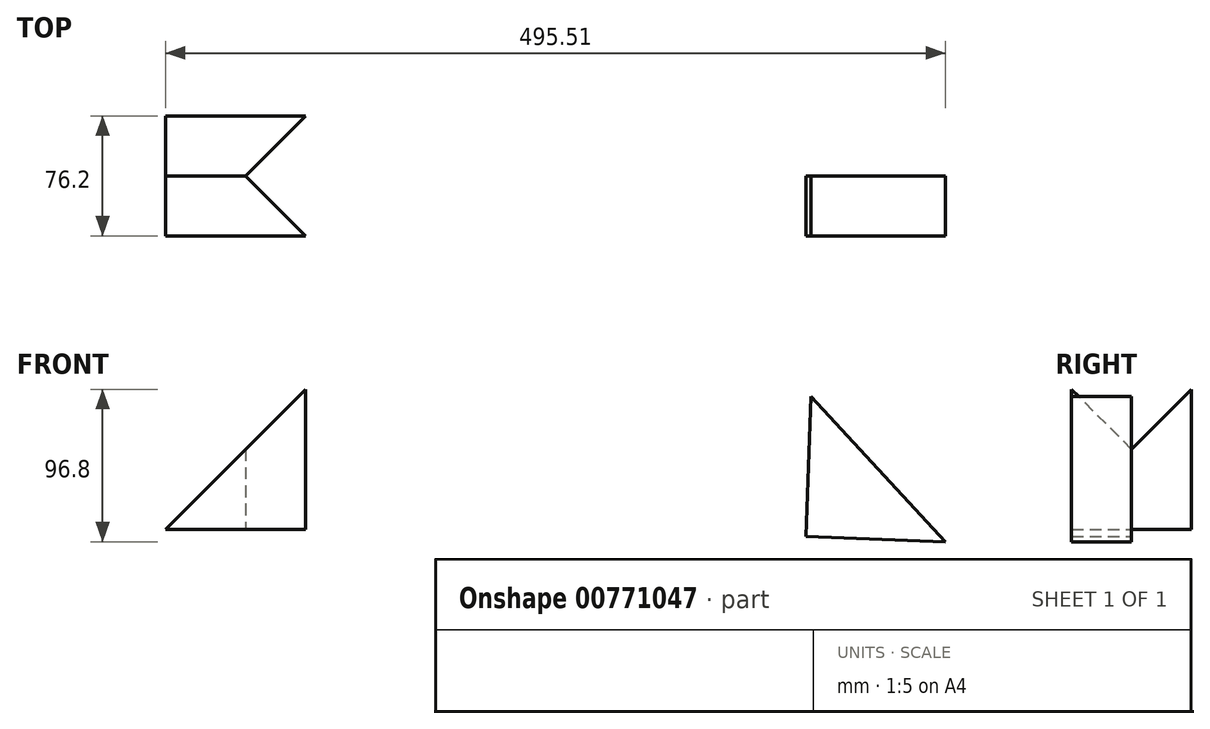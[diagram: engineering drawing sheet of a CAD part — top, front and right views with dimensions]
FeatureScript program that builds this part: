
annotation { "Feature Type Name" : "Feature", "Feature Type Description" : "" }
export const myFeature = defineFeature(function(context is Context, id is Id, definition is map)
    precondition{}
    {
        {
            var Q0;
            Q0=qCreatedBy(makeId("Front.planeOp"),FACE);
            var sketch = newSketch(context, id + "F0", { "sketchPlane" : qUnion([Q0])});
            skLineSegment(sketch, "E0", {"start": v(66.82, 257.53) * mm, "end": v(155.72, 257.53) * mm});
            skLineSegment(sketch, "E1", {"start": v(155.72, 257.53) * mm, "end": v(155.72, 346.43) * mm});
            skLineSegment(sketch, "E2", {"start": v(155.72, 346.43) * mm, "end": v(66.82, 257.53) * mm});
            skSolve(sketch);
        }
        {
            var Q0;
            Q0=makeQuery(id+"F0.imprint","IMPRINT",FACE,{"disambiguationData":[TD([[makeQuery(id+"F0.imprint","IMPRINT",EDGE,{"derivedFrom":sQuery(id+"F0.wireOp",EDGE,"E0")}),1.0]])]});
            extrude(context, id + "F1", {"entities" : qUnion([Q0]), "depth" : 38.1 * mm, "offsetDistance" : 25.4 * mm});
        }
        {
            var Q0;
            Q0=qCreatedBy(makeId("Front.planeOp"),FACE);
            var sketch = newSketch(context, id + "F2", { "sketchPlane" : qUnion([Q0])});
            skLineSegment(sketch, "E3", {"start": v(219.24, 257.56) * mm, "end": v(205.65, 358.25) * mm});
            skLineSegment(sketch, "E4", {"start": v(205.65, 358.25) * mm, "end": v(319.93, 271.16) * mm});
            skLineSegment(sketch, "E5", {"start": v(319.93, 271.16) * mm, "end": v(219.24, 257.56) * mm});
            skSolve(sketch);
        }
        {
            var Q0;
            Q0=qSketchRegion(id+"F2",true);
            extrude(context, id + "F3", {"entities" : qUnion([Q0]), "depth" : 38.1 * mm, "offsetDistance" : 25.4 * mm});
        }
        {
            var Q0;
            Q0=qCreatedBy(makeId("Front.planeOp"),FACE);
            var sketch = newSketch(context, id + "F4", { "sketchPlane" : qUnion([Q0])});
            skLineSegment(sketch, "E6", {"start": v(476.84, 341.81) * mm, "end": v(473.49, 252.98) * mm});
            skLineSegment(sketch, "E7", {"start": v(473.49, 252.98) * mm, "end": v(562.33, 249.63) * mm});
            skLineSegment(sketch, "E8", {"start": v(562.33, 249.63) * mm, "end": v(476.84, 341.81) * mm});
            skSolve(sketch);
        }
        {
            var Q0;
            Q0=qSketchRegion(id+"F4",true);
            extrude(context, id + "F5", {"entities" : qUnion([Q0]), "depth" : 38.1 * mm, "offsetDistance" : 25.4 * mm});
        }
        {
            var Q0;
            Q0=makeQuery(id+"F3.opExtrude","SWEPT_FACE",FACE,{"disambiguationData":[OSD([sQuery(id+"F2.wireOp",EDGE,"E5")])]});
            var sketch = newSketch(context, id + "F6", { "sketchPlane" : qUnion([Q0])});
            skLineSegment(sketch, "E9", {"start": v(251.75, 38.1) * mm, "end": v(289.85, 0) * mm});
            skLineSegment(sketch, "E10", {"start": v(289.85, 0) * mm, "end": v(251.75, 0) * mm});
            skLineSegment(sketch, "E11", {"start": v(251.75, 0) * mm, "end": v(251.75, 38.1) * mm});
            skSolve(sketch);
        }
        {
            var Q0;
            Q0=makeQuery(id+"F6.imprint","IMPRINT",FACE,{"disambiguationData":[TD([[makeQuery(id+"F6.imprint","IMPRINT",EDGE,{"derivedFrom":sQuery(id+"F6.wireOp",EDGE,"E9")}),-1.0]])]});
            extrude(context, id + "F7", {"entities" : qUnion([Q0]), "operationType" : NewBodyOperationType.REMOVE, "endBound" : BoundingType.THROUGH_ALL, "oppositeDirection" : true, "depth" : 25.4 * mm, "offsetDistance" : 25.4 * mm});
        }
        {
            var Q0;
            Q0=makeQuery(id+"F1.opExtrude","SWEPT_FACE",FACE,{"disambiguationData":[OSD([sQuery(id+"F0.wireOp",EDGE,"E0")])]});
            var sketch = newSketch(context, id + "F8", { "sketchPlane" : qUnion([Q0])});
            skLineSegment(sketch, "E12", {"start": v(155.72, 38.1) * mm, "end": v(155.72, 0) * mm});
            skLineSegment(sketch, "E13", {"start": v(155.72, 0) * mm, "end": v(117.62, 0) * mm});
            skLineSegment(sketch, "E14", {"start": v(117.62, 0) * mm, "end": v(155.72, 38.1) * mm});
            skSolve(sketch);
        }
        {
            var Q0;
            Q0=qSketchRegion(id+"F8",true);
            extrude(context, id + "F9", {"entities" : qUnion([Q0]), "operationType" : NewBodyOperationType.REMOVE, "endBound" : BoundingType.THROUGH_ALL, "oppositeDirection" : true, "depth" : 25.4 * mm, "offsetDistance" : 25.4 * mm});
        }
        {
            var Q0;
            Q0=makeQuery(id+"F3.opExtrude","SWEPT_BODY",BODY,{"disambiguationData":[OSD([sQuery(id+"F2.wireOp",EDGE,"E3"),sQuery(id+"F2.wireOp",EDGE,"E4"),sQuery(id+"F2.wireOp",EDGE,"E5")])]});
            deleteBodies(context, id + "F10", {"entities" : qUnion([Q0])});
        }
        {
            var Q0;
            Q0=makeQuery(id+"F1.opExtrude","SWEPT_BODY",BODY,{"disambiguationData":[OSD([sQuery(id+"F0.wireOp",EDGE,"E0"),sQuery(id+"F0.wireOp",EDGE,"E1"),sQuery(id+"F0.wireOp",EDGE,"E2")])]});
            var Q1;
            Q1=qCreatedBy(makeId("Front.planeOp"),FACE);
            mirror(context, id + "F11", {"entities" : qUnion([Q0]), "mirrorPlane" : qUnion([Q1])});
        }
    });
